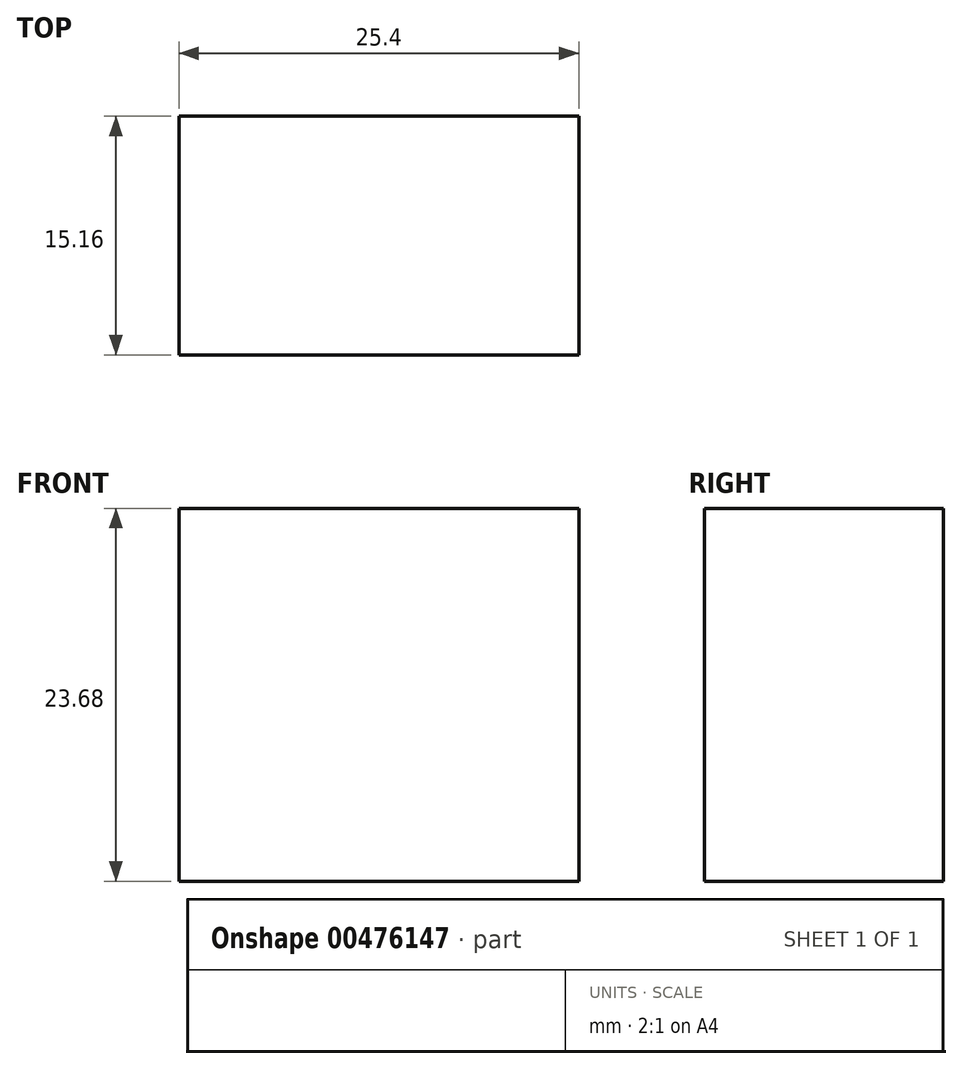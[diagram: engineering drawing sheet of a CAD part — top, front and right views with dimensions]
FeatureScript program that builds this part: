
annotation { "Feature Type Name" : "Feature", "Feature Type Description" : "" }
export const myFeature = defineFeature(function(context is Context, id is Id, definition is map)
    precondition{}
    {
        {
            var Q0;
            Q0=qCreatedBy(makeId("Right.planeOp"),FACE);
            var sketch = newSketch(context, id + "F0", { "sketchPlane" : qUnion([Q0])});
            skLineSegment(sketch, "E0.bottom", {"start": v(-28.53, 0) * mm, "end": v(-13.37, 0) * mm});
            skLineSegment(sketch, "E0.top", {"start": v(-28.53, 23.68) * mm, "end": v(-13.37, 23.68) * mm});
            skLineSegment(sketch, "E0.left", {"start": v(-28.53, 0) * mm, "end": v(-28.53, 23.68) * mm});
            skLineSegment(sketch, "E0.right", {"start": v(-13.37, 0) * mm, "end": v(-13.37, 23.68) * mm});
            skSolve(sketch);
        }
        {
            var Q0;
            Q0 = qSketchRegion(id + "F0", true);
            extrude(context, id + "F1", {"entities" : qUnion([Q0]), "depth" : 25.4 * mm});
        }
    });
